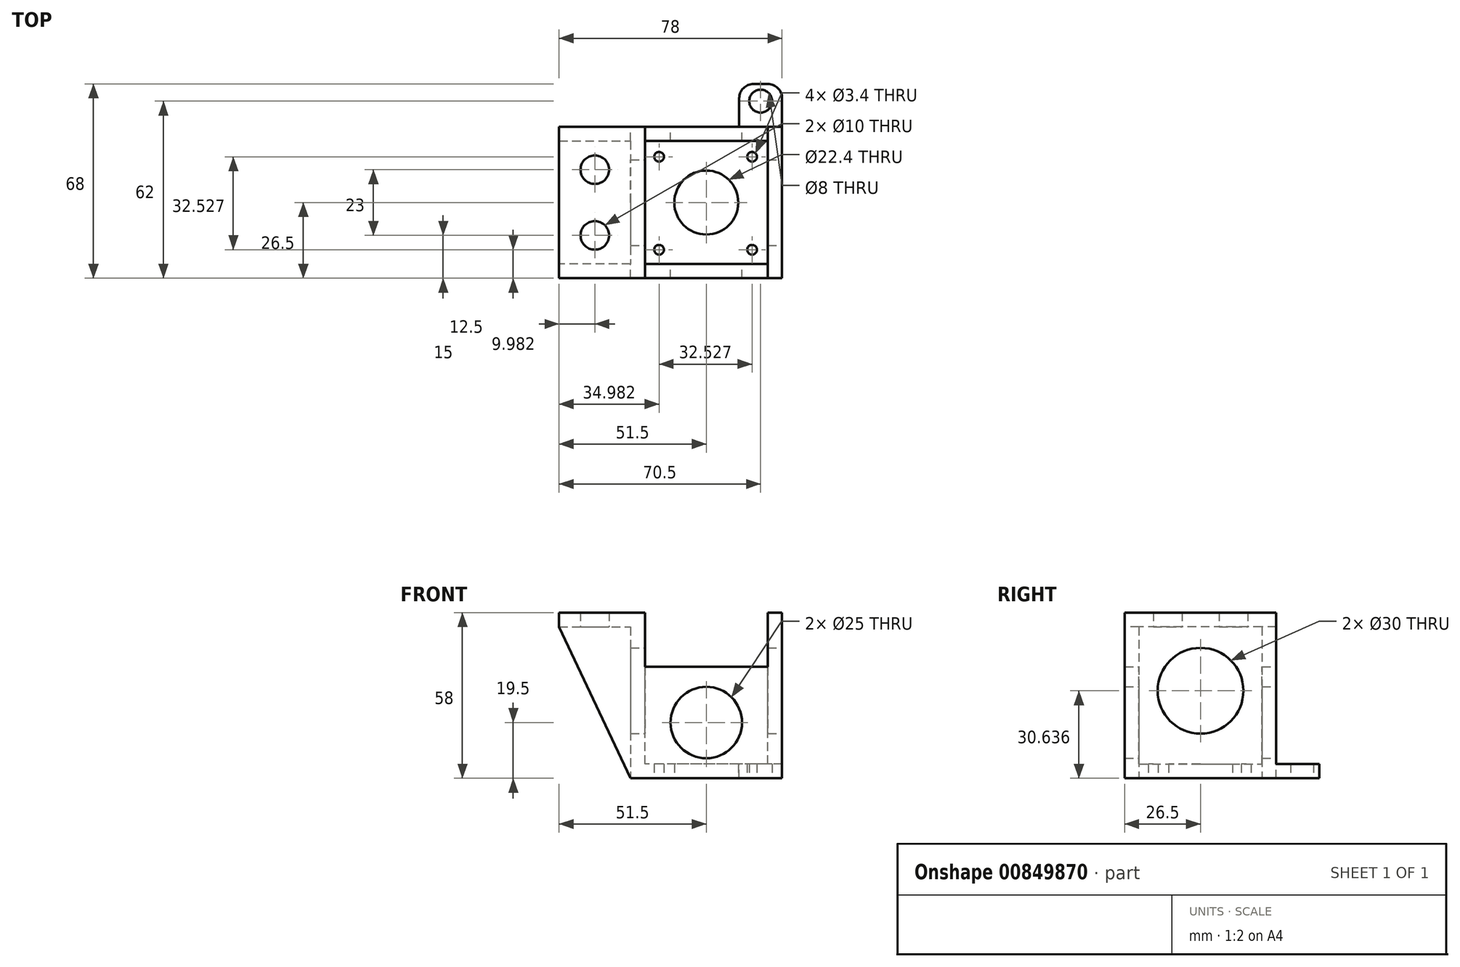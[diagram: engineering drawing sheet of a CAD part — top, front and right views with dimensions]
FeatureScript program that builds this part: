
annotation { "Feature Type Name" : "Feature", "Feature Type Description" : "" }
export const myFeature = defineFeature(function(context is Context, id is Id, definition is map)
    precondition{}
    {
        {
            var Q0;
            Q0=qCreatedBy(makeId("Top.planeOp"),FACE);
            var sketch = newSketch(context, id + "F0", { "sketchPlane" : qUnion([Q0])});
            skLineSegment(sketch, "E0.bottom", {"start": v(26.5, -26.5) * mm, "end": v(-26.5, -26.5) * mm});
            skLineSegment(sketch, "E0.top", {"start": v(26.5, 26.5) * mm, "end": v(-26.5, 26.5) * mm});
            skLineSegment(sketch, "E0.left", {"start": v(26.5, -26.5) * mm, "end": v(26.5, 26.5) * mm});
            skLineSegment(sketch, "E0.right", {"start": v(-26.5, -26.5) * mm, "end": v(-26.5, 26.5) * mm});
            skPoint(sketch, "E0.middle", {"position": v(0, 0) * mm});
            skSolve(sketch);
        }
        {
            var Q0;
            Q0=makeQuery(id+"F0.imprint","IMPRINT",FACE,{"disambiguationData":[TD([[makeQuery(id+"F0.imprint","IMPRINT",EDGE,{"derivedFrom":sQuery(id+"F0.wireOp",EDGE,"E0.bottom")}),-1.0]])]});
            extrude(context, id + "F1", {"entities" : qUnion([Q0]), "depth" : 10 * mm, "offsetDistance" : 25 * mm});
        }
        {
            var Q0;
            Q0=makeQuery(id+"F1.opExtrude","CAP_FACE",FACE,{"disambiguationData":[OSD([sQuery(id+"F0.wireOp",EDGE,"E0.bottom"),sQuery(id+"F0.wireOp",EDGE,"E0.top"),sQuery(id+"F0.wireOp",EDGE,"E0.left"),sQuery(id+"F0.wireOp",EDGE,"E0.right")])],"isStart":false});
            var sketch = newSketch(context, id + "F2", { "sketchPlane" : qUnion([Q0])});
            skLineSegment(sketch, "E1.bottom", {"start": v(21.5, -21.5) * mm, "end": v(-21.5, -21.5) * mm});
            skLineSegment(sketch, "E1.top", {"start": v(21.5, 21.5) * mm, "end": v(-21.5, 21.5) * mm});
            skLineSegment(sketch, "E1.left", {"start": v(21.5, -21.5) * mm, "end": v(21.5, 21.5) * mm});
            skLineSegment(sketch, "E1.right", {"start": v(-21.5, -21.5) * mm, "end": v(-21.5, 21.5) * mm});
            skPoint(sketch, "E1.middle", {"position": v(0, 0) * mm});
            skSolve(sketch);
        }
        {
            var Q0;
            Q0=makeQuery(id+"F2.imprint","IMPRINT",FACE,{"disambiguationData":[TD([[makeQuery(id+"F2.imprint","IMPRINT",EDGE,{"derivedFrom":sQuery(id+"F2.wireOp",EDGE,"E1.bottom")}),-1.0]])]});
            extrude(context, id + "F3", {"entities" : qUnion([Q0]), "operationType" : NewBodyOperationType.REMOVE, "oppositeDirection" : true, "depth" : 5 * mm, "offsetDistance" : 25 * mm});
        }
        {
            var Q0;
            Q0=makeQuery(id+"F1.opExtrude","CAP_FACE",FACE,{"disambiguationData":[OSD([sQuery(id+"F0.wireOp",EDGE,"E0.bottom"),sQuery(id+"F0.wireOp",EDGE,"E0.top"),sQuery(id+"F0.wireOp",EDGE,"E0.left"),sQuery(id+"F0.wireOp",EDGE,"E0.right")])],"isStart":true});
            var sketch = newSketch(context, id + "F4", { "sketchPlane" : qUnion([Q0])});
            skLineSegment(sketch, "E2", {"start": v(-26.5, 26.5) * mm, "end": v(26.5, -26.5) * mm, "construction": true});
            skCircle(sketch, "E3", {"center": v(-16.52, 16.52) * mm, "radius": 1.7 * mm});
            skCircle(sketch, "E4.1.0", {"center": v(-16.52, -16) * mm, "radius": 1.7 * mm});
            skCircle(sketch, "E4.2.0", {"center": v(16, -16) * mm, "radius": 1.7 * mm});
            skCircle(sketch, "E4.3.0", {"center": v(16, 16.52) * mm, "radius": 1.7 * mm});
            skPoint(sketch, "E4.center", {"position": v(-0.25, 0.25) * mm});
            skSolve(sketch);
        }
        {
            var Q0;
            Q0=makeQuery(id+"F4.imprint","IMPRINT",FACE,{"disambiguationData":[TD([[makeQuery(id+"F4.imprint","IMPRINT",EDGE,{"derivedFrom":sQuery(id+"F4.wireOp",EDGE,"E3")}),1.0]])]});
            var Q1;
            Q1=makeQuery(id+"F4.imprint","IMPRINT",FACE,{"disambiguationData":[TD([[makeQuery(id+"F4.imprint","IMPRINT",EDGE,{"derivedFrom":sQuery(id+"F4.wireOp",EDGE,"E4.3.0")}),1.0]])]});
            var Q2;
            Q2=makeQuery(id+"F4.imprint","IMPRINT",FACE,{"disambiguationData":[TD([[makeQuery(id+"F4.imprint","IMPRINT",EDGE,{"derivedFrom":sQuery(id+"F4.wireOp",EDGE,"E4.2.0")}),1.0]])]});
            var Q3;
            Q3=makeQuery(id+"F4.imprint","IMPRINT",FACE,{"disambiguationData":[TD([[makeQuery(id+"F4.imprint","IMPRINT",EDGE,{"derivedFrom":sQuery(id+"F4.wireOp",EDGE,"E4.1.0")}),1.0]])]});
            extrude(context, id + "F5", {"entities" : qUnion([Q0, Q1, Q2, Q3]), "operationType" : NewBodyOperationType.REMOVE, "oppositeDirection" : true, "depth" : 25 * mm, "offsetDistance" : 25 * mm});
        }
        {
            var Q0;
            Q0=makeQuery(id+"F1.opExtrude","CAP_FACE",FACE,{"disambiguationData":[OSD([sQuery(id+"F0.wireOp",EDGE,"E0.bottom"),sQuery(id+"F0.wireOp",EDGE,"E0.top"),sQuery(id+"F0.wireOp",EDGE,"E0.left"),sQuery(id+"F0.wireOp",EDGE,"E0.right")])],"isStart":true});
            var sketch = newSketch(context, id + "F6", { "sketchPlane" : qUnion([Q0])});
            skCircle(sketch, "E5", {"center": v(0, 0) * mm, "radius": 11.2 * mm});
            skSolve(sketch);
        }
        {
            var Q0;
            Q0=makeQuery(id+"F6.imprint","IMPRINT",FACE,{"disambiguationData":[TD([[makeQuery(id+"F6.imprint","IMPRINT",EDGE,{"derivedFrom":sQuery(id+"F6.wireOp",EDGE,"E5")}),1.0]])]});
            extrude(context, id + "F7", {"entities" : qUnion([Q0]), "operationType" : NewBodyOperationType.REMOVE, "oppositeDirection" : true, "depth" : 25 * mm, "offsetDistance" : 25 * mm});
        }
        {
            var Q0;
            Q0=makeQuery(id+"F1.opExtrude","CAP_FACE",FACE,{"disambiguationData":[OSD([sQuery(id+"F0.wireOp",EDGE,"E0.bottom"),sQuery(id+"F0.wireOp",EDGE,"E0.top"),sQuery(id+"F0.wireOp",EDGE,"E0.left"),sQuery(id+"F0.wireOp",EDGE,"E0.right")])],"isStart":false});
            var sketch = newSketch(context, id + "F8", { "sketchPlane" : qUnion([Q0])});
            skLineSegment(sketch, "E6", {"start": v(-21.5, 21.5) * mm, "end": v(-21.5, 26.5) * mm});
            skLineSegment(sketch, "E7", {"start": v(21.5, 21.5) * mm, "end": v(21.5, 26.5) * mm});
            skLineSegment(sketch, "E8", {"start": v(-21.5, -21.5) * mm, "end": v(-21.5, -26.5) * mm});
            skLineSegment(sketch, "E9", {"start": v(21.5, -21.5) * mm, "end": v(21.5, -26.5) * mm});
            skSolve(sketch);
        }
        {
            var Q0;
            {var subQ2=sQuery(id+"F8.wireOp",EDGE,"E6");Q0=makeQuery(id+"F8.imprint","IMPRINT",FACE,{"disambiguationData":[TD([[makeQuery(id+"F8.imprint","IMPRINT",EDGE,{"derivedFrom":subQ2}),1.0]])]});}
            var Q1;
            {var subQ2=sQuery(id+"F8.wireOp",EDGE,"E7");Q1=makeQuery(id+"F8.imprint","IMPRINT",FACE,{"disambiguationData":[TD([[makeQuery(id+"F8.imprint","IMPRINT",EDGE,{"derivedFrom":subQ2}),-1.0]])]});}
            extrude(context, id + "F9", {"entities" : qUnion([Q0, Q1]), "operationType" : NewBodyOperationType.ADD, "depth" : 48 * mm, "offsetDistance" : 25 * mm});
        }
        {
            var Q0;
            {var subQ3=sQuery(id+"F0.wireOp",EDGE,"E0.top");var subQ5=sQuery(id+"F0.wireOp",EDGE,"E0.left");var subQ7=sQuery(id+"F0.wireOp",EDGE,"E0.right");Q0=makeQuery(id+"F9.boolean.opBoolean","SPLIT",FACE,{"disambiguationData":[TD([makeQuery(id+"F1.opExtrude","SWEPT_FACE",FACE,{"disambiguationData":[OSD([subQ3])]})])],"derivedFrom":makeQuery(id+"F1.opExtrude","CAP_FACE",FACE,{"disambiguationData":[OSD([sQuery(id+"F0.wireOp",EDGE,"E0.bottom"),subQ3,subQ5,subQ7])],"isStart":false})});}
            var Q1;
            {var subQ2=sQuery(id+"F0.wireOp",EDGE,"E0.bottom");var subQ5=sQuery(id+"F0.wireOp",EDGE,"E0.left");var subQ7=sQuery(id+"F0.wireOp",EDGE,"E0.right");Q1=makeQuery(id+"F9.boolean.opBoolean","SPLIT",FACE,{"disambiguationData":[TD([makeQuery(id+"F1.opExtrude","SWEPT_FACE",FACE,{"disambiguationData":[OSD([subQ2])]})])],"derivedFrom":makeQuery(id+"F1.opExtrude","CAP_FACE",FACE,{"disambiguationData":[OSD([subQ2,sQuery(id+"F0.wireOp",EDGE,"E0.top"),subQ5,subQ7])],"isStart":false})});}
            extrude(context, id + "F10", {"entities" : qUnion([Q0, Q1]), "operationType" : NewBodyOperationType.ADD, "depth" : 29 * mm, "offsetDistance" : 25 * mm});
        }
        {
            var Q0;
            {var subQ0=sQuery(id+"F0.wireOp",EDGE,"E0.left");Q0=makeQuery(id+"F9.boolean.opBoolean","MERGE",FACE,{"derivedFrom":[makeQuery(id+"F1.opExtrude","SWEPT_FACE",FACE,{"disambiguationData":[OSD([subQ0])]}),makeQuery(id+"F9.opExtrude","SWEPT_FACE",FACE,{"disambiguationData":[OSD([subQ0])]})]});}
            var sketch = newSketch(context, id + "F11", { "sketchPlane" : qUnion([Q0])});
            skCircle(sketch, "E10", {"center": v(0, 30.64) * mm, "radius": 15 * mm});
            skSolve(sketch);
        }
        {
            var Q0;
            Q0=makeQuery(id+"F11.imprint","IMPRINT",FACE,{"disambiguationData":[TD([[makeQuery(id+"F11.imprint","IMPRINT",EDGE,{"derivedFrom":sQuery(id+"F11.wireOp",EDGE,"E10")}),1.0]])]});
            extrude(context, id + "F12", {"entities" : qUnion([Q0]), "operationType" : NewBodyOperationType.REMOVE, "endBound" : BoundingType.THROUGH_ALL, "oppositeDirection" : true, "depth" : 25 * mm, "offsetDistance" : 25 * mm});
        }
        {
            var Q0;
            {var subQ0=sQuery(id+"F0.wireOp",EDGE,"E0.top");var subQ1=makeQuery(id+"F1.opExtrude","CAP_EDGE",EDGE,{"disambiguationData":[OSD([subQ0])],"isStart":false});Q0=makeQuery(id+"F10.boolean.opBoolean","MERGE",FACE,{"derivedFrom":[makeQuery(id+"F9.boolean.opBoolean","MERGE",FACE,{"derivedFrom":[makeQuery(id+"F1.opExtrude","SWEPT_FACE",FACE,{"disambiguationData":[OSD([subQ0])]}),makeQuery(id+"F9.opExtrude","SWEPT_FACE",FACE,{"disambiguationData":[OSD([subQ0]),TDD([makeQuery(id+"F8.imprint","IMPRINT",EDGE,{"disambiguationData":[TD([[makeQuery(id+"F8.imprint","INTERSECT",VERTEX,{"derivedFrom":[subQ1,makeQuery(id+"F1.opExtrude","CAP_EDGE",EDGE,{"disambiguationData":[OSD([sQuery(id+"F0.wireOp",EDGE,"E0.left")])],"isStart":false})]}),-1.0]])],"derivedFrom":subQ1})])]}),makeQuery(id+"F9.opExtrude","SWEPT_FACE",FACE,{"disambiguationData":[OSD([subQ0]),TDD([makeQuery(id+"F8.imprint","IMPRINT",EDGE,{"disambiguationData":[TD([[makeQuery(id+"F8.imprint","INTERSECT",VERTEX,{"derivedFrom":[subQ1,makeQuery(id+"F1.opExtrude","CAP_EDGE",EDGE,{"disambiguationData":[OSD([sQuery(id+"F0.wireOp",EDGE,"E0.right")])],"isStart":false})]}),1.0]])],"derivedFrom":subQ1})])]})]}),makeQuery(id+"F10.opExtrude","SWEPT_FACE",FACE,{"disambiguationData":[OSD([subQ0])]})]});}
            var sketch = newSketch(context, id + "F13", { "sketchPlane" : qUnion([Q0])});
            skCircle(sketch, "E11", {"center": v(0, 19.5) * mm, "radius": 12.5 * mm});
            skSolve(sketch);
        }
        {
            var Q0;
            Q0=makeQuery(id+"F13.imprint","IMPRINT",FACE,{"disambiguationData":[TD([[makeQuery(id+"F13.imprint","IMPRINT",EDGE,{"derivedFrom":sQuery(id+"F13.wireOp",EDGE,"E11")}),1.0]])]});
            extrude(context, id + "F14", {"entities" : qUnion([Q0]), "operationType" : NewBodyOperationType.REMOVE, "endBound" : BoundingType.THROUGH_ALL, "oppositeDirection" : true, "depth" : 25 * mm, "offsetDistance" : 25 * mm});
        }
        {
            var Q0;
            {var subQ0=sQuery(id+"F0.wireOp",EDGE,"E0.right");Q0=makeQuery(id+"F9.boolean.opBoolean","MERGE",FACE,{"derivedFrom":[makeQuery(id+"F1.opExtrude","SWEPT_FACE",FACE,{"disambiguationData":[OSD([subQ0])]}),makeQuery(id+"F9.opExtrude","SWEPT_FACE",FACE,{"disambiguationData":[OSD([subQ0])]})]});}
            var sketch = newSketch(context, id + "F15", { "sketchPlane" : qUnion([Q0])});
            skLineSegment(sketch, "E12.bottom", {"start": v(-26.5, 58) * mm, "end": v(-21.5, 58) * mm});
            skLineSegment(sketch, "E12.top", {"start": v(-26.5, 0) * mm, "end": v(-21.5, 0) * mm});
            skLineSegment(sketch, "E12.left", {"start": v(-26.5, 58) * mm, "end": v(-26.5, 0) * mm});
            skLineSegment(sketch, "E12.right", {"start": v(-21.5, 58) * mm, "end": v(-21.5, 0) * mm});
            skLineSegment(sketch, "E13.bottom", {"start": v(26.5, 58) * mm, "end": v(21.5, 58) * mm});
            skLineSegment(sketch, "E13.top", {"start": v(26.5, 0) * mm, "end": v(21.5, 0) * mm});
            skLineSegment(sketch, "E13.left", {"start": v(26.5, 58) * mm, "end": v(26.5, 0) * mm});
            skLineSegment(sketch, "E13.right", {"start": v(21.5, 58) * mm, "end": v(21.5, 0) * mm});
            skSolve(sketch);
        }
        {
            var Q0;
            Q0=makeQuery(id+"F15.imprint","IMPRINT",FACE,{"disambiguationData":[TD([[makeQuery(id+"F15.imprint","IMPRINT",EDGE,{"derivedFrom":sQuery(id+"F15.wireOp",EDGE,"E12.bottom")}),1.0]])]});
            var Q1;
            Q1=makeQuery(id+"F15.imprint","IMPRINT",FACE,{"disambiguationData":[TD([[makeQuery(id+"F15.imprint","IMPRINT",EDGE,{"derivedFrom":sQuery(id+"F15.wireOp",EDGE,"E13.bottom")}),1.0]])]});
            extrude(context, id + "F16", {"entities" : qUnion([Q0, Q1]), "operationType" : NewBodyOperationType.ADD, "depth" : 25 * mm, "offsetDistance" : 25 * mm});
        }
        {
            var Q0;
            Q0=makeQuery(id+"F16.opExtrude","CAP_EDGE",EDGE,{"disambiguationData":[OSD([sQuery(id+"F15.wireOp",EDGE,"E12.top")])],"isStart":false});
            var Q1;
            Q1=makeQuery(id+"F16.opExtrude","CAP_EDGE",EDGE,{"disambiguationData":[OSD([sQuery(id+"F15.wireOp",EDGE,"E13.top")])],"isStart":false});
            chamfer(context, id + "F17", {"entities" : qUnion([Q0, Q1]), "chamferType" : ChamferType.TWO_OFFSETS, "width1" : 25 * mm, "oppositeDirection" : false, "width2" : 53 * mm, "tangentPropagation" : true});
        }
        {
            var Q0;
            {var subQ0=sQuery(id+"F0.wireOp",EDGE,"E0.right");Q0=makeQuery(id+"F9.boolean.opBoolean","MERGE",FACE,{"derivedFrom":[makeQuery(id+"F1.opExtrude","SWEPT_FACE",FACE,{"disambiguationData":[OSD([subQ0])]}),makeQuery(id+"F9.opExtrude","SWEPT_FACE",FACE,{"disambiguationData":[OSD([subQ0])]})]});}
            var sketch = newSketch(context, id + "F18", { "sketchPlane" : qUnion([Q0])});
            skLineSegment(sketch, "E14.bottom", {"start": v(-21.5, 58) * mm, "end": v(21.5, 58) * mm});
            skLineSegment(sketch, "E14.top", {"start": v(-21.5, 53) * mm, "end": v(21.5, 53) * mm});
            skLineSegment(sketch, "E14.left", {"start": v(-21.5, 58) * mm, "end": v(-21.5, 53) * mm});
            skLineSegment(sketch, "E14.right", {"start": v(21.5, 58) * mm, "end": v(21.5, 53) * mm});
            skSolve(sketch);
        }
        {
            var Q0;
            Q0=makeQuery(id+"F18.imprint","IMPRINT",FACE,{"disambiguationData":[TD([[makeQuery(id+"F18.imprint","IMPRINT",EDGE,{"derivedFrom":sQuery(id+"F18.wireOp",EDGE,"E14.bottom")}),1.0]])]});
            extrude(context, id + "F19", {"entities" : qUnion([Q0]), "operationType" : NewBodyOperationType.ADD, "depth" : 25 * mm, "offsetDistance" : 25 * mm});
        }
        {
            var Q0;
            Q0=makeQuery(id+"F19.opExtrude","SWEPT_FACE",FACE,{"disambiguationData":[OSD([sQuery(id+"F18.wireOp",EDGE,"E14.top")])]});
            var sketch = newSketch(context, id + "F20", { "sketchPlane" : qUnion([Q0])});
            skCircle(sketch, "E15", {"center": v(-39, 11.5) * mm, "radius": 5 * mm});
            skCircle(sketch, "E16", {"center": v(-39, -11.5) * mm, "radius": 5 * mm});
            skSolve(sketch);
        }
        {
            var Q0;
            Q0=makeQuery(id+"F20.imprint","IMPRINT",FACE,{"disambiguationData":[TD([[makeQuery(id+"F20.imprint","IMPRINT",EDGE,{"derivedFrom":sQuery(id+"F20.wireOp",EDGE,"E15")}),1.0]])]});
            var Q1;
            Q1=makeQuery(id+"F20.imprint","IMPRINT",FACE,{"disambiguationData":[TD([[makeQuery(id+"F20.imprint","IMPRINT",EDGE,{"derivedFrom":sQuery(id+"F20.wireOp",EDGE,"E16")}),1.0]])]});
            extrude(context, id + "F21", {"entities" : qUnion([Q0, Q1]), "operationType" : NewBodyOperationType.REMOVE, "oppositeDirection" : true, "depth" : 25 * mm, "offsetDistance" : 25 * mm});
        }
        {
            var Q0;
            {var subQ0=sQuery(id+"F15.wireOp",EDGE,"E12.left");var subQ1=sQuery(id+"F0.wireOp",EDGE,"E0.top");var subQ2=makeQuery(id+"F1.opExtrude","CAP_EDGE",EDGE,{"disambiguationData":[OSD([subQ1])],"isStart":false});Q0=makeQuery(id+"F9RaZhJXookUSdu_1.1.F16.boolean.opBoolean","MERGE",FACE,{"derivedFrom":[makeQuery(id+"F16.boolean.opBoolean","MERGE",FACE,{"derivedFrom":[makeQuery(id+"F10.boolean.opBoolean","MERGE",FACE,{"derivedFrom":[makeQuery(id+"F9.boolean.opBoolean","MERGE",FACE,{"derivedFrom":[makeQuery(id+"F1.opExtrude","SWEPT_FACE",FACE,{"disambiguationData":[OSD([subQ1])]}),makeQuery(id+"F9.opExtrude","SWEPT_FACE",FACE,{"disambiguationData":[OSD([subQ1]),TDD([makeQuery(id+"F8.imprint","IMPRINT",EDGE,{"disambiguationData":[TD([[makeQuery(id+"F8.imprint","INTERSECT",VERTEX,{"derivedFrom":[subQ2,makeQuery(id+"F1.opExtrude","CAP_EDGE",EDGE,{"disambiguationData":[OSD([sQuery(id+"F0.wireOp",EDGE,"E0.left")])],"isStart":false})]}),-1.0]])],"derivedFrom":subQ2})])]}),makeQuery(id+"F9.opExtrude","SWEPT_FACE",FACE,{"disambiguationData":[OSD([subQ1]),TDD([makeQuery(id+"F8.imprint","IMPRINT",EDGE,{"disambiguationData":[TD([[makeQuery(id+"F8.imprint","INTERSECT",VERTEX,{"derivedFrom":[subQ2,makeQuery(id+"F1.opExtrude","CAP_EDGE",EDGE,{"disambiguationData":[OSD([sQuery(id+"F0.wireOp",EDGE,"E0.right")])],"isStart":false})]}),1.0]])],"derivedFrom":subQ2})])]})]}),makeQuery(id+"F10.opExtrude","SWEPT_FACE",FACE,{"disambiguationData":[OSD([subQ1])]})]}),makeQuery(id+"F16.opExtrude","SWEPT_FACE",FACE,{"disambiguationData":[OSD([subQ0])]})]}),makeQuery(id+"F9RaZhJXookUSdu_1.1.F16.opExtrude","SWEPT_FACE",FACE,{"disambiguationData":[OSD([subQ0])]})]});}
            var sketch = newSketch(context, id + "F22", { "sketchPlane" : qUnion([Q0])});
            skLineSegment(sketch, "E17.bottom", {"start": v(-26.5, 0) * mm, "end": v(-11.5, 0) * mm});
            skLineSegment(sketch, "E17.top", {"start": v(-26.5, 5) * mm, "end": v(-11.5, 5) * mm});
            skLineSegment(sketch, "E17.left", {"start": v(-26.5, 0) * mm, "end": v(-26.5, 5) * mm});
            skLineSegment(sketch, "E17.right", {"start": v(-11.5, 0) * mm, "end": v(-11.5, 5) * mm});
            skSolve(sketch);
        }
        {
            var Q0;
            Q0=makeQuery(id+"F22.imprint","IMPRINT",FACE,{"disambiguationData":[TD([[makeQuery(id+"F22.imprint","IMPRINT",EDGE,{"derivedFrom":sQuery(id+"F22.wireOp",EDGE,"E17.bottom")}),1.0]])]});
            extrude(context, id + "F23", {"entities" : qUnion([Q0]), "operationType" : NewBodyOperationType.ADD, "depth" : 15 * mm, "offsetDistance" : 25 * mm});
        }
        {
            var Q0;
            Q0=makeQuery(id+"F23.opExtrude","CAP_EDGE",EDGE,{"disambiguationData":[OSD([sQuery(id+"F22.wireOp",EDGE,"E17.right")])],"isStart":false});
            var Q1;
            Q1=makeQuery(id+"F23.opExtrude","CAP_EDGE",EDGE,{"disambiguationData":[OSD([sQuery(id+"F22.wireOp",EDGE,"E17.left")])],"isStart":false});
            fillet(context, id + "F24", {"entities" : qUnion([Q0, Q1]), "radius" : 5 * mm, "tangentPropagation" : true, "allowEdgeOverflow" : false});
        }
        {
            var Q0;
            {var subQ0=sQuery(id+"F22.wireOp",EDGE,"E17.bottom");var subQ1=sQuery(id+"F15.wireOp",EDGE,"E13.top");var subQ2=sQuery(id+"F15.wireOp",EDGE,"E12.top");Q0=makeQuery(id+"FA6L9372NBbwUHe_1.1.F23.boolean.opBoolean","MERGE",FACE,{"derivedFrom":[makeQuery(id+"F23.boolean.opBoolean","MERGE",FACE,{"derivedFrom":[makeQuery(id+"F9RaZhJXookUSdu_1.1.F16.boolean.opBoolean","MERGE",FACE,{"derivedFrom":[makeQuery(id+"F16.boolean.opBoolean","MERGE",FACE,{"derivedFrom":[makeQuery(id+"F1.opExtrude","CAP_FACE",FACE,{"disambiguationData":[OSD([sQuery(id+"F0.wireOp",EDGE,"E0.bottom"),sQuery(id+"F0.wireOp",EDGE,"E0.top"),sQuery(id+"F0.wireOp",EDGE,"E0.left"),sQuery(id+"F0.wireOp",EDGE,"E0.right")])],"isStart":true}),makeQuery(id+"F16.opExtrude","SWEPT_FACE",FACE,{"disambiguationData":[OSD([subQ2])]}),makeQuery(id+"F16.opExtrude","SWEPT_FACE",FACE,{"disambiguationData":[OSD([subQ1])]})]}),makeQuery(id+"F9RaZhJXookUSdu_1.1.F16.opExtrude","SWEPT_FACE",FACE,{"disambiguationData":[OSD([subQ2])]}),makeQuery(id+"F9RaZhJXookUSdu_1.1.F16.opExtrude","SWEPT_FACE",FACE,{"disambiguationData":[OSD([subQ1])]})]}),makeQuery(id+"F23.opExtrude","SWEPT_FACE",FACE,{"disambiguationData":[OSD([subQ0])]})]}),makeQuery(id+"FA6L9372NBbwUHe_1.1.F23.opExtrude","SWEPT_FACE",FACE,{"disambiguationData":[OSD([subQ0])]})]});}
            var sketch = newSketch(context, id + "F25", { "sketchPlane" : qUnion([Q0])});
            skCircle(sketch, "E18", {"center": v(19, -35.5) * mm, "radius": 4 * mm});
            skSolve(sketch);
        }
        {
            var Q0;
            Q0=makeQuery(id+"F25.imprint","IMPRINT",FACE,{"disambiguationData":[TD([[makeQuery(id+"F25.imprint","IMPRINT",EDGE,{"derivedFrom":sQuery(id+"F25.wireOp",EDGE,"E18")}),1.0]])]});
            extrude(context, id + "F26", {"entities" : qUnion([Q0]), "operationType" : NewBodyOperationType.REMOVE, "oppositeDirection" : true, "depth" : 25 * mm, "offsetDistance" : 25 * mm});
        }
    });
